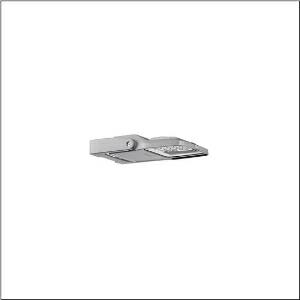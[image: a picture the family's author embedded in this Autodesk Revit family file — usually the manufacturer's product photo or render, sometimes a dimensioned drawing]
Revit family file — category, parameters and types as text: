
# Revit family: floodlight_fl_21_iq_micro___pl33t_5xa7761a2f2a_98c0
name_source: partatom
category: Lighting Fixtures
units: mm (PartAtom-declared; Revit-internal decimal feet)

## family parameters
Cut with Voids When Loaded = No
Host = Face
Light Source = No
Part Type = Normal
Room Calculation Point = No
Round Connector Dimension = Use Diameter
Shared = No

## types (1)
- --- (1 x LED, 2930 lm, 23.1 W, 3000K)
    Apparent Load = 23 VA
    CIE Flux Codes = 26 75 99 100 100
    Color Rendering = 70
    Color Temperature = 3000K
    Default Elevation = 1800 mm
    Description = Floodlight FL 21 iQ micro, floodlight, primary light control with lens, of PMMA, primary optical cover: protective disc, of toughened safety glass, transparent, light distribution: PL33T, light emission: direct distribution, installation type: surface-mounted, lamps: LED, High Power LED, rated values: 2.930lm | 23,1W | 126,8lm/W (begin service life); end service life: 2.930lm | 23,8W; at 50% lumin. flux: 1.465lm | 11W | 133,2lm/W, colour temperature: 3000K, colour rendering: CRI > 70, light colour: 730, light setting 1 begin service life: 100% | 2.930lm | 23,1W | 126,8lm/W | 3.000K, light setting 1 end service life: 23,8W, further light settings possible, control: optimised constant luminous flux control (CLO 2.0), Desk-Remote (wireless, voltage-free reading and setting of iQ features in the workshop via application-optimized NFC function/RFID function), Light-Fading, Smart-Wire, Night-Set, Lumen-Switch, Temp-Guard, Auto-Match, pre-setting: linear dimming characteristic, with terminal, 6-pole, mains connection: 220..240V, AC, 50/60Hz, luminaire housing, of diecast aluminium, powder-coated, SITECO metallic grey (DB 702S), corrosivity category C5 mid according to DIN EN ISO 12944suitable for swimming poolschlorine-resistant, sealing non-destructively replaceable, design bracket, of diecast aluminium, powder-coated, SITECO metallic grey (DB 702S), protection rating (complete): IP66, insulation class (complete): insulation class II (safety insulation), certification: CE, ENEC, VDE, protection symbol: D, impact resistance: IK07, permissible operating ambient temperature: -40..+40°C, permissible operating ambient temperature for outdoor applications: -40..+50°C, standard: DIN EN 12944, LABS conformity tested according to VDMA 24364:2018-05, packaging unit: 1 piece

Light Distribution: PL33T
    Height = 65 mm
    Lamp = 1 x LED
    Lamp Light Flux = 2930 lm
    Lamp Power = 23.1 W
    Lamp count = 1
    Length = 312 mm
    Luminous efficacy = 127 lm/W
    Manufacturer = Siteco
    ModVariant = No
    Model = 5XA7761A2F2A
    Mounting Place = Wall
    Mounting Type = Surface mounted
    Number of Poles = 1
    OnlyDefault = Yes
    Power Factor = 1
    Product Name = Floodlight FL 21 iQ micro | PL33T
    Product group = floodlight | wall mounted
    ProductGroupID = 2002
    Protection Class = Protection class II
    Protection Degree = IP 66
    RLX_Detail_Level = 1
    RLX_Emergency_Light_Flux = 0 lm
    RLX_Emergency_Type = 0
    RLX_Emergency_Type_DB = No
    RlxData = <blob elided: 97481 chars, md5=89388d1c>
    Socket = socket
    Standby Power = 0 W
    System Light Flux = 2930 lm
    System Power = 23 W
    Type Comments = factory setting: luminous flux: 100 % | dim-lin: 254 | 455 mA
    Type Image = l_1006878.jpg
    URL = http://relux.com
    VarID = @adj_147749
    Voltage = 0 V
    Weight = 0.00 kg
    Width = 230 mm

## geometry (parser evidence)
native form markers: Blend x4, Sweep x14
no freeform markers — native parametric forms only
